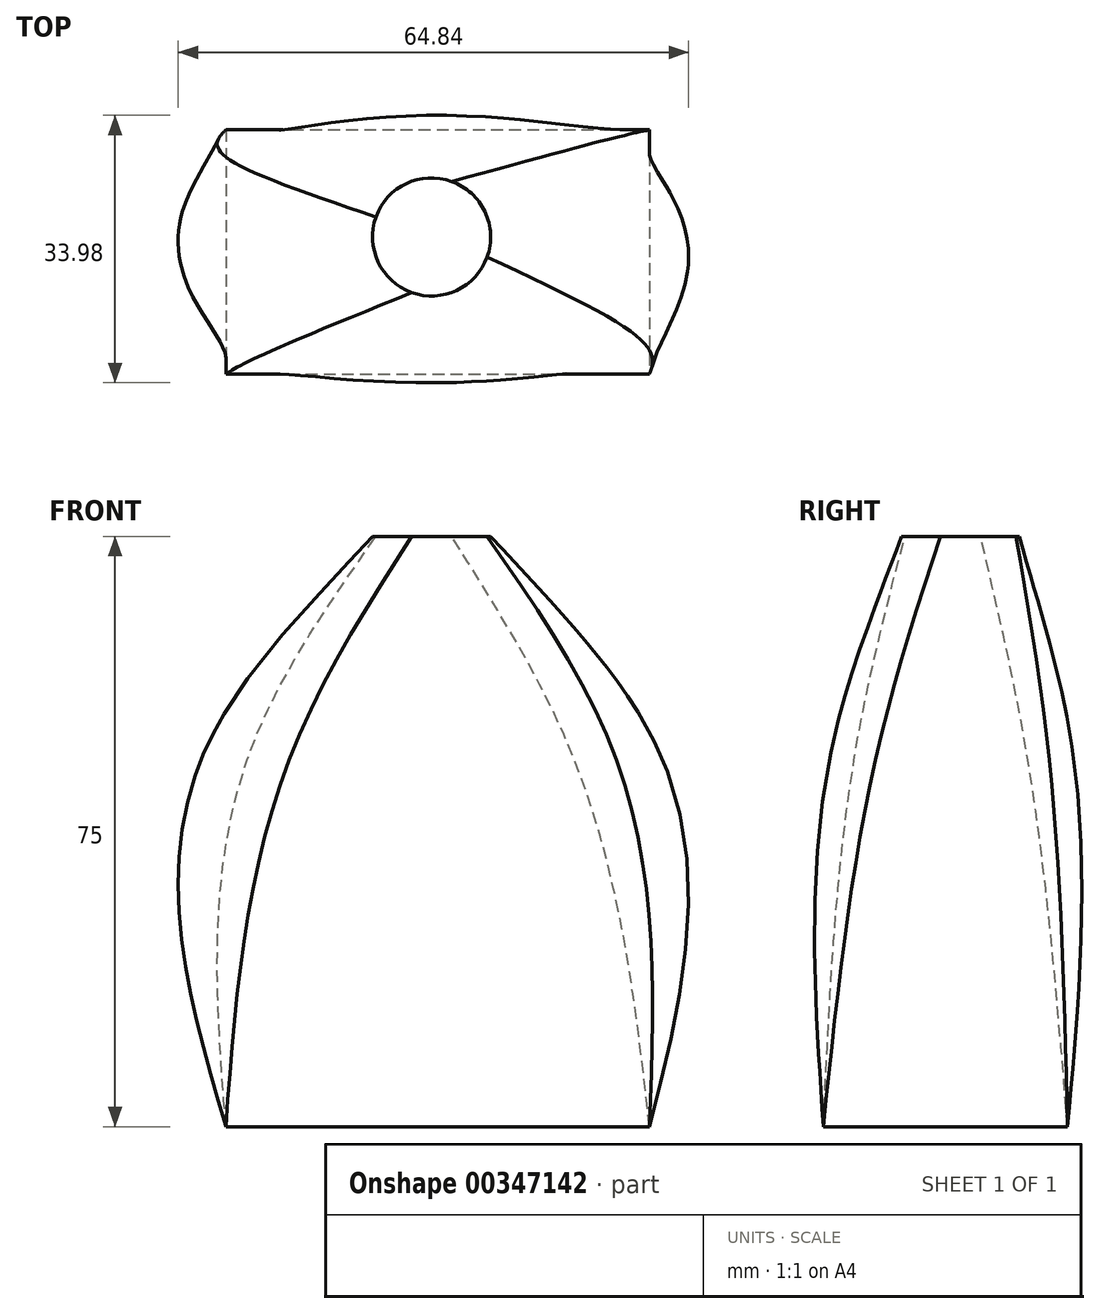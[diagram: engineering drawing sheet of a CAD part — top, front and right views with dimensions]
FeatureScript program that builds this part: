
annotation { "Feature Type Name" : "Feature", "Feature Type Description" : "" }
export const myFeature = defineFeature(function(context is Context, id is Id, definition is map)
    precondition{}
    {
        {
            var Q0;
            Q0=qCreatedBy(makeId("Top.planeOp"),FACE);
            var sketch = newSketch(context, id + "F0", { "sketchPlane" : qUnion([Q0])});
            skLineSegment(sketch, "E0.bottom", {"start": v(-26.14, 9.74) * mm, "end": v(27.68, 9.74) * mm});
            skLineSegment(sketch, "E0.top", {"start": v(-26.14, -21.27) * mm, "end": v(27.68, -21.27) * mm});
            skLineSegment(sketch, "E0.left", {"start": v(-26.14, 9.74) * mm, "end": v(-26.14, -21.27) * mm});
            skLineSegment(sketch, "E0.right", {"start": v(27.68, 9.74) * mm, "end": v(27.68, -21.27) * mm});
            skSolve(sketch);
        }
        {
            var Q0;
            Q0=qCreatedBy(makeId("Top.planeOp"),FACE);
            cPlane(context, id + "F1", {"entities" : qUnion([Q0]), "cplaneType" : CPlaneType.OFFSET, "offset" : 50 * mm, "width" : 150 * mm, "height" : 150 * mm});
        }
        {
            var Q0;
            Q0=qCreatedBy(id+"F1.planeOp",FACE);
            var sketch = newSketch(context, id + "F2", { "sketchPlane" : qUnion([Q0])});
            skEllipse(sketch, "E1", {"center": v(0, -4.88) * mm, "majorRadius": 27.73 * mm, "minorRadius": 14.92 * mm, "majorAxis": v(-1, 0)});
            skSolve(sketch);
        }
        {
            var Q0;
            Q0=qCreatedBy(id+"F1.planeOp",FACE);
            cPlane(context, id + "F3", {"entities" : qUnion([Q0]), "cplaneType" : CPlaneType.OFFSET, "offset" : 25 * mm, "width" : 150 * mm, "height" : 150 * mm});
        }
        {
            var Q0;
            Q0=qCreatedBy(id+"F3.planeOp",FACE);
            var sketch = newSketch(context, id + "F4", { "sketchPlane" : qUnion([Q0])});
            skPoint(sketch, "E2.first.point", {"position": v(0, -5.49) * mm});
            skPoint(sketch, "E2.second.point", {"position": v(-13.4, -7.92) * mm});
            skPoint(sketch, "E2.third.point", {"position": v(0, 0) * mm});
            skCircle(sketch, "E3", {"center": v(-0.01, -3.87) * mm, "radius": 7.5 * mm});
            skPoint(sketch, "E3.second.point", {"position": v(7.31, -5.49) * mm});
            skPoint(sketch, "E3.third.point", {"position": v(6.1, -8.23) * mm});
            skSolve(sketch);
        }
        {
            var Q0;
            Q0=makeQuery(id+"F0.imprint","IMPRINT",FACE,{"disambiguationData":[TD([[makeQuery(id+"F0.imprint","IMPRINT",EDGE,{"derivedFrom":sQuery(id+"F0.wireOp",EDGE,"E0.bottom")}),-1.0]])]});
            var Q1;
            Q1=makeQuery(id+"F2.imprint","IMPRINT",FACE,{"disambiguationData":[TD([[makeQuery(id+"F2.imprint","IMPRINT",EDGE,{"derivedFrom":sQuery(id+"F2.wireOp",EDGE,"E1")}),1.0]])]});
            var Q2;
            Q2=makeQuery(id+"F4.imprint","IMPRINT",FACE,{"disambiguationData":[TD([[makeQuery(id+"F4.imprint","IMPRINT",EDGE,{"derivedFrom":sQuery(id+"F4.wireOp",EDGE,"E3")}),1.0]])]});
            loft(context, id + "F5", {"sheetProfilesArray" : [{ "sheetProfileEntities" : qUnion([Q0]) }, { "sheetProfileEntities" : qUnion([Q1]) }, { "sheetProfileEntities" : qUnion([Q2]) }]});
        }
    });
